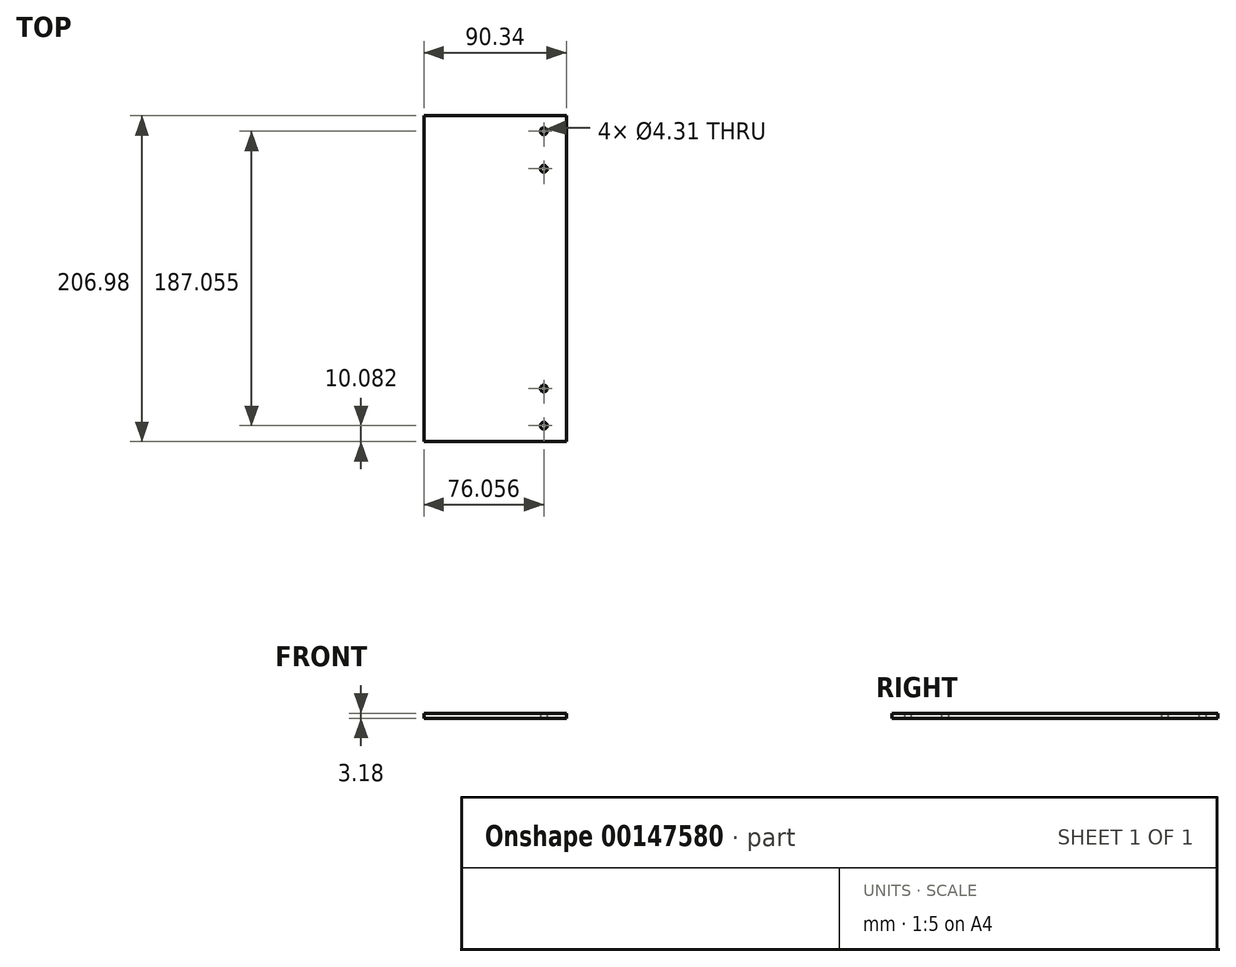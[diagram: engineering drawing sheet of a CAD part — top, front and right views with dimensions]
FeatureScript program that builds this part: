
annotation { "Feature Type Name" : "Feature", "Feature Type Description" : "" }
export const myFeature = defineFeature(function(context is Context, id is Id, definition is map)
    precondition{}
    {
        {
            var Q0;
            Q0=qCreatedBy(makeId("Top.planeOp"),FACE);
            var sketch = newSketch(context, id + "F0", { "sketchPlane" : qUnion([Q0])});
            skPoint(sketch, "E0.rect.middle", {"position": v(0, 0) * mm});
            skLineSegment(sketch, "E1.bottom", {"start": v(90.34, -206.98) * mm, "end": v(0, -206.98) * mm});
            skLineSegment(sketch, "E1.top", {"start": v(90.34, 0) * mm, "end": v(0, 0) * mm});
            skLineSegment(sketch, "E1.left", {"start": v(90.34, -206.98) * mm, "end": v(90.34, 0) * mm});
            skLineSegment(sketch, "E1.right", {"start": v(0, -206.98) * mm, "end": v(0, 0) * mm});
            skLineSegment(sketch, "E2", {"start": v(0, 0) * mm, "end": v(0, 0) * mm});
            skLineSegment(sketch, "E3.right", {"start": v(76.06, -33.72) * mm, "end": v(76.06, -173.27) * mm, "construction": true});
            skCircle(sketch, "E4", {"center": v(76.06, -33.72) * mm, "radius": 2.15 * mm});
            skCircle(sketch, "E5", {"center": v(76.06, -173.27) * mm, "radius": 2.15 * mm});
            skLineSegment(sketch, "E6", {"start": v(76.06, -33.72) * mm, "end": v(76.06, -9.84) * mm, "construction": true});
            skLineSegment(sketch, "E7", {"start": v(76.06, -173.27) * mm, "end": v(76.06, -196.9) * mm, "construction": true});
            skCircle(sketch, "E8", {"center": v(76.06, -9.84) * mm, "radius": 2.15 * mm});
            skCircle(sketch, "E9", {"center": v(76.06, -196.9) * mm, "radius": 2.15 * mm});
            skLineSegment(sketch, "E10", {"start": v(76.06, -9.84) * mm, "end": v(76.06, 0) * mm, "construction": true});
            skLineSegment(sketch, "E11", {"start": v(90.34, -103.5) * mm, "end": v(76.06, -103.5) * mm, "construction": true});
            skSolve(sketch);
        }
        {
            var Q0;
            Q0=qSketchRegion(id+"F0",true);
            extrude(context, id + "F1", {"entities" : qUnion([Q0]), "depth" : 3.17 * mm});
        }
    });
